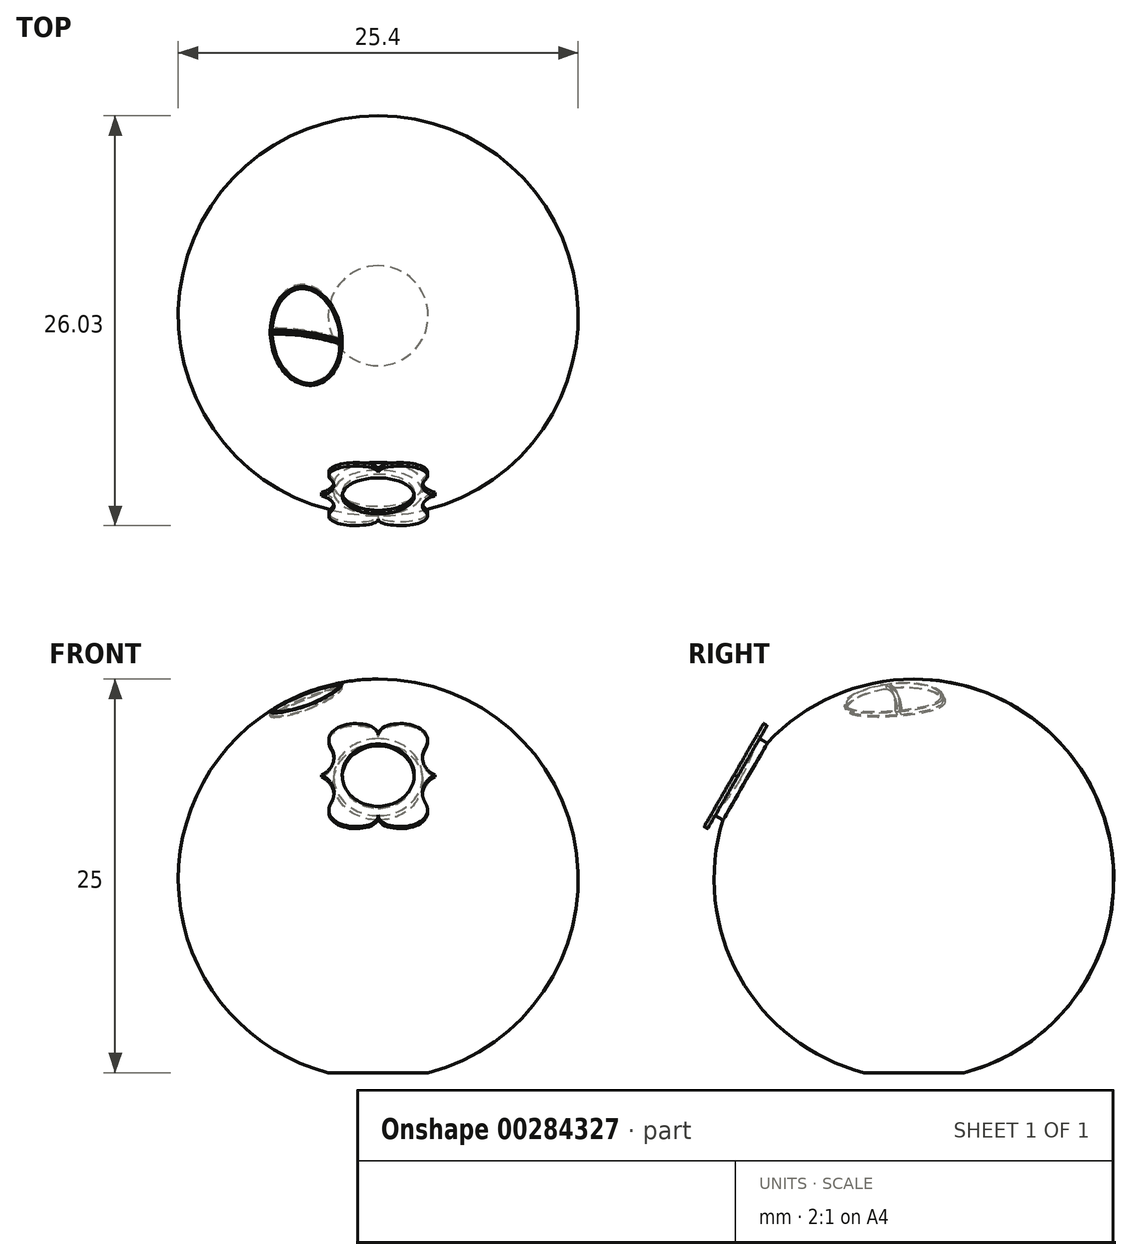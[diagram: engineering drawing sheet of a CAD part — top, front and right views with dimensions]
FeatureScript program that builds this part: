
annotation { "Feature Type Name" : "Feature", "Feature Type Description" : "" }
export const myFeature = defineFeature(function(context is Context, id is Id, definition is map)
    precondition{}
    {
        {
            var Q0;
            Q0=qCreatedBy(makeId("Right.planeOp"),FACE);
            var sketch = newSketch(context, id + "F0", { "sketchPlane" : qUnion([Q0])});
            skArc(sketch, "E0", {"start": v(3.18, 0) * mm, "mid": v(0, 25) * mm, "end": v(-3.18, 0) * mm});
            skLineSegment(sketch, "E1", {"start": v(3.18, 0) * mm, "end": v(-3.18, 0) * mm});
            skLineSegment(sketch, "E2", {"start": v(0, 25) * mm, "end": v(0, 0) * mm});
            skLineSegment(sketch, "E3", {"start": v(-11, 18.65) * mm, "end": v(-11.44, 18.9) * mm});
            skLineSegment(sketch, "E4", {"start": v(-11.44, 18.9) * mm, "end": v(-12.85, 16.46) * mm});
            skLineSegment(sketch, "E5", {"start": v(-12.85, 16.46) * mm, "end": v(-12.13, 16.04) * mm});
            skLineSegment(sketch, "E6", {"start": v(-12.58, 16.92) * mm, "end": v(-12.36, 16.8) * mm});
            skArc(sketch, "E7", {"start": v(-12.36, 16.8) * mm, "mid": v(-11.64, 17.7) * mm, "end": v(-11.02, 18.66) * mm});
            skLineSegment(sketch, "E8", {"start": v(-11.02, 18.66) * mm, "end": v(-12.43, 16.22) * mm, "construction": true});
            skLineSegment(sketch, "E9", {"start": v(-4.55, 24.15) * mm, "end": v(0, 12.3) * mm, "construction": true});
            skArc(sketch, "E10.0", {"start": v(3.11, 0.25) * mm, "mid": v(0, 24.74) * mm, "end": v(-3.11, 0.25) * mm});
            skLineSegment(sketch, "E11", {"start": v(-3.11, 0.25) * mm, "end": v(3.11, 0.25) * mm});
            skSolve(sketch);
        }
        {
            var Q0;
            {var subQ3=sQuery(id+"F0.wireOp",EDGE,"E2");Q0=makeQuery(id+"F0.imprint","IMPRINT",FACE,{"disambiguationData":[TD([[makeQuery(id+"F0.imprint","IMPRINT",EDGE,{"derivedFrom":subQ3}),-1.0]])]});}
            var Q1;
            {var subQ0=sQuery(id+"F0.wireOp",EDGE,"E10.0");var subQ1=sQuery(id+"F0.wireOp",EDGE,"E2");var subQ2=makeQuery(id+"F0.imprint","INTERSECT",VERTEX,{"derivedFrom":[subQ1,subQ0]});Q1=makeQuery(id+"F0.imprint","IMPRINT",FACE,{"disambiguationData":[TD([[makeQuery(id+"F0.imprint","IMPRINT",EDGE,{"disambiguationData":[TD([[subQ2,-1.0]])],"derivedFrom":subQ1}),-1.0]])]});}
            var Q2;
            Q2=sQuery(id+"F0.wireOp",EDGE,"E2");
            revolve(context, id + "F1", {"entities" : qUnion([Q0, Q1]), "axis" : qUnion([Q2]), "revolveType" : RevolveType.FULL});
        }
        {
            var Q0;
            {var subQ1=sQuery(id+"F0.wireOp",EDGE,"E5");Q0=makeQuery(id+"F0.imprint","IMPRINT",FACE,{"disambiguationData":[TD([[makeQuery(id+"F0.imprint","IMPRINT",EDGE,{"derivedFrom":subQ1}),1.0]])]});}
            var Q1;
            {var subQ4=sQuery(id+"F0.wireOp",EDGE,"E6");Q1=makeQuery(id+"F0.imprint","IMPRINT",FACE,{"disambiguationData":[TD([[makeQuery(id+"F0.imprint","IMPRINT",EDGE,{"derivedFrom":subQ4}),1.0]])]});}
            var Q2;
            Q2=sQuery(id+"F0.wireOp",EDGE,"E3");
            revolve(context, id + "F2", {"operationType" : NewBodyOperationType.ADD, "entities" : qUnion([Q0, Q1]), "axis" : qUnion([Q2]), "revolveType" : RevolveType.FULL});
        }
        {
            var Q0;
            Q0=makeQuery(id+"F2.opRevolve","SWEPT_FACE",FACE,{"disambiguationData":[OSD([sQuery(id+"F0.wireOp",EDGE,"E4")])]});
            var sketch = newSketch(context, id + "F3", { "sketchPlane" : qUnion([Q0])});
            skLineSegment(sketch, "E12", {"start": v(0, 10.65) * mm, "end": v(-3.6, 10.65) * mm});
            skLineSegment(sketch, "E13", {"start": v(0, 10.65) * mm, "end": v(0, 13.59) * mm});
            skArc(sketch, "E14", {"start": v(-3.6, 10.65) * mm, "mid": v(-2.88, 11.52) * mm, "end": v(-2.98, 12.65) * mm});
            skLineSegment(sketch, "E15", {"start": v(-3.6, 10.65) * mm, "end": v(0, 12.55) * mm});
            skLineSegment(sketch, "E16", {"start": v(-2.98, 12.65) * mm, "end": v(-2.29, 11.34) * mm, "construction": true});
            skFitSpline(sketch, "E17", {"points": [v(-2.98, 12.65) * mm, v(-2.15, 14.32) * mm, v(0, 13.59) * mm], "startDerivative": vector(-2.55, 4.82) * mm, "endDerivative": vector(0, -4.4) * mm});
            skSolve(sketch);
        }
        {
            var Q0;
            {var subQ1=sQuery(id+"F3.wireOp",EDGE,"E14");Q0=makeQuery(id+"F3.imprint","IMPRINT",FACE,{"disambiguationData":[TD([[makeQuery(id+"F3.imprint","IMPRINT",EDGE,{"derivedFrom":subQ1}),-1.0]])]});}
            var Q1;
            {var subQ0=sQuery(id+"F3.wireOp",EDGE,"E15");var subQ1=sQuery(id+"F3.wireOp",EDGE,"E12");var subQ2=makeQuery(id+"F3.imprint","INTERSECT",VERTEX,{"derivedFrom":[subQ1,sQuery(id+"F3.wireOp",EDGE,"E14"),subQ0]});Q1=makeQuery(id+"F3.imprint","IMPRINT",FACE,{"disambiguationData":[TD([[makeQuery(id+"F3.imprint","IMPRINT",EDGE,{"disambiguationData":[TD([[subQ2,1.0]])],"derivedFrom":subQ1}),-1.0]])]});}
            extrude(context, id + "F4", {"entities" : qUnion([Q0, Q1]), "oppositeDirection" : true, "depth" : 0.25 * mm});
        }
        {
            var Q0;
            Q0=makeQuery(id+"F4.opExtrude","SWEPT_BODY",BODY,{"disambiguationData":[OSD([sQuery(id+"F0.wireOp",EDGE,"E4"),sQuery(id+"F0.wireOp",EDGE,"E5"),sQuery(id+"F3.wireOp",EDGE,"E12"),sQuery(id+"F3.wireOp",EDGE,"E13"),sQuery(id+"F3.wireOp",EDGE,"E14"),sQuery(id+"F3.wireOp",EDGE,"E17")])]});
            var Q1;
            Q1=makeQuery(id+"Fticf5Y9S86viFH_1.opRevolve","SWEPT_BODY",BODY,{"disambiguationData":[OSD([sQuery(id+"F0.wireOp",EDGE,"E4"),sQuery(id+"F0.wireOp",EDGE,"E6"),sQuery(id+"F3.wireOp",EDGE,"E13"),sQuery(id+"F3.wireOp",EDGE,"E14"),sQuery(id+"F3.wireOp",EDGE,"E15"),sQuery(id+"F3.wireOp",EDGE,"E17")])]});
            var Q2;
            Q2=makeQuery(id+"F4.opExtrude","SWEPT_FACE",FACE,{"disambiguationData":[OSD([sQuery(id+"F3.wireOp",EDGE,"E12")])]});
            mirror(context, id + "F5", {"entities" : qUnion([Q0, Q1]), "mirrorPlane" : qUnion([Q2])});
        }
        {
            var Q0;
            Q0=makeQuery(id+"F4.opExtrude","SWEPT_BODY",BODY,{"disambiguationData":[OSD([sQuery(id+"F0.wireOp",EDGE,"E4"),sQuery(id+"F0.wireOp",EDGE,"E5"),sQuery(id+"F3.wireOp",EDGE,"E12"),sQuery(id+"F3.wireOp",EDGE,"E13"),sQuery(id+"F3.wireOp",EDGE,"E14"),sQuery(id+"F3.wireOp",EDGE,"E17")])]});
            var Q1;
            Q1=makeQuery(id+"F5.opPattern","COPY",BODY,{"derivedFrom":makeQuery(id+"F4.opExtrude","SWEPT_BODY",BODY,{"disambiguationData":[OSD([sQuery(id+"F0.wireOp",EDGE,"E4"),sQuery(id+"F0.wireOp",EDGE,"E5"),sQuery(id+"F3.wireOp",EDGE,"E12"),sQuery(id+"F3.wireOp",EDGE,"E13"),sQuery(id+"F3.wireOp",EDGE,"E14"),sQuery(id+"F3.wireOp",EDGE,"E17")])]}),"instanceName":"1"});
            var Q2;
            Q2=makeQuery(id+"F5.opPattern","COPY",BODY,{"derivedFrom":makeQuery(id+"Fticf5Y9S86viFH_1.opRevolve","SWEPT_BODY",BODY,{"disambiguationData":[OSD([sQuery(id+"F0.wireOp",EDGE,"E4"),sQuery(id+"F0.wireOp",EDGE,"E5"),sQuery(id+"F3.wireOp",EDGE,"E13"),sQuery(id+"F3.wireOp",EDGE,"E14"),sQuery(id+"F3.wireOp",EDGE,"E15"),sQuery(id+"F3.wireOp",EDGE,"E17")])]}),"instanceName":"1"});
            var Q3;
            Q3=makeQuery(id+"Fticf5Y9S86viFH_1.opRevolve","SWEPT_BODY",BODY,{"disambiguationData":[OSD([sQuery(id+"F0.wireOp",EDGE,"E4"),sQuery(id+"F0.wireOp",EDGE,"E5"),sQuery(id+"F3.wireOp",EDGE,"E13"),sQuery(id+"F3.wireOp",EDGE,"E14"),sQuery(id+"F3.wireOp",EDGE,"E15"),sQuery(id+"F3.wireOp",EDGE,"E17")])]});
            var Q4;
            Q4=qCreatedBy(makeId("Right.planeOp"),FACE);
            mirror(context, id + "F6", {"operationType" : NewBodyOperationType.ADD, "entities" : qUnion([Q0, Q1, Q2, Q3]), "mirrorPlane" : qUnion([Q4])});
        }
        {
            var Q0;
            {var subQ4=sQuery(id+"F0.wireOp",EDGE,"E6");Q0=makeQuery(id+"F0.imprint","IMPRINT",FACE,{"disambiguationData":[TD([[makeQuery(id+"F0.imprint","IMPRINT",EDGE,{"derivedFrom":subQ4}),1.0]])]});}
            var Q1;
            Q1=sQuery(id+"F0.wireOp",EDGE,"E3");
            revolve(context, id + "F7", {"operationType" : NewBodyOperationType.REMOVE, "entities" : qUnion([Q0]), "axis" : qUnion([Q1]), "revolveType" : RevolveType.FULL, "oppositeDirection" : true});
        }
        {
            var Q0;
            Q0=sQuery(id+"F0.wireOp",EDGE,"E9");
            var Q1;
            Q1=sQuery(id+"F0.wireOp",VERTEX,"E9.start");
            cPlane(context, id + "F8", {"entities" : qUnion([Q0, Q1]), "cplaneType" : CPlaneType.LINE_POINT, "offset" : 25.4 * mm, "width" : 152.4 * mm, "height" : 152.4 * mm});
        }
        {
            var Q0;
            Q0=qCreatedBy(id+"F8.planeOp",FACE);
            var sketch = newSketch(context, id + "F9", { "sketchPlane" : qUnion([Q0])});
            skCircle(sketch, "E18", {"center": v(-4.57, -7.28) * mm, "radius": 3.05 * mm, "construction": true});
            skArc(sketch, "E19", {"start": v(-1.65, -7.15) * mm, "mid": v(-4.57, -4.36) * mm, "end": v(-7.5, -7.15) * mm, "construction": true});
            skLineSegment(sketch, "E20", {"start": v(-7.5, -7.4) * mm, "end": v(-1.65, -7.4) * mm, "construction": true});
            skLineSegment(sketch, "E21", {"start": v(-1.65, -7.15) * mm, "end": v(-7.5, -7.15) * mm, "construction": true});
            skLineSegment(sketch, "E22", {"start": v(-4.57, -7.4) * mm, "end": v(-4.57, -7.15) * mm, "construction": true});
            skArc(sketch, "E23.trimOffspring", {"start": v(-7.5, -7.4) * mm, "mid": v(-4.57, -10.2) * mm, "end": v(-1.65, -7.4) * mm, "construction": true});
            skCircle(sketch, "E24", {"center": v(-4.16, -9.44) * mm, "radius": 0.38 * mm});
            skLineSegment(sketch, "E25", {"start": v(0, -0.57) * mm, "end": v(0, -11.54) * mm, "construction": true});
            skCircle(sketch, "E26", {"center": v(4.57, -7.28) * mm, "radius": 3.05 * mm});
            skLineSegment(sketch, "E27", {"start": v(-4.57, -7.28) * mm, "end": v(4.57, -7.28) * mm, "construction": true});
            skPoint(sketch, "E28", {"position": v(0, -7.28) * mm});
            skCircle(sketch, "E29", {"center": v(4.99, -9.44) * mm, "radius": 0.38 * mm});
            skLineSegment(sketch, "E30", {"start": v(-4.16, -9.44) * mm, "end": v(4.99, -9.44) * mm, "construction": true});
            skArc(sketch, "E31", {"start": v(-1.65, -7.4) * mm, "mid": v(-4.57, -7.15) * mm, "end": v(-7.5, -7.4) * mm, "construction": true});
            skArc(sketch, "E32", {"start": v(-1.65, -7.15) * mm, "mid": v(-4.57, -6.9) * mm, "end": v(-7.5, -7.15) * mm, "construction": true});
            skEllipse(sketch, "E33", {"center": v(-4.57, -7.28) * mm, "majorRadius": 3.05 * mm, "minorRadius": 2.29 * mm, "majorAxis": v(0, 1)});
            skEllipticalArc(sketch, "E34", {});
            skArc(sketch, "E35", {"start": v(-6.73, -7.4) * mm, "mid": v(-4.57, -7.66) * mm, "end": v(-2.42, -7.4) * mm});
            skArc(sketch, "E36", {"start": v(-6.73, -7.15) * mm, "mid": v(-4.57, -7.4) * mm, "end": v(-2.42, -7.15) * mm});
            skEllipticalArc(sketch, "E37.trimOffspring", {});
            skEllipticalArc(sketch, "E38.trimOffspring", {});
            const initialGuessF9  = {"E34": [-0.004572, -0.007277323653828481, 0, -1, 0.002921, 0.002159, 4.755880951174804, 1.5273043560047805], "E37.trimOffspring": [-0.004572, -0.007277323653828481, 0, -1, 0.002921, 0.002159, 1.6142882975850121, 4.668897009594579], "E38.trimOffspring": [-0.004572, -0.007277323653828481, 0, -1, 0.002921, 0.002159, 1.5668431296332357, 1.5707963267948966]};
            skSetInitialGuess(sketch, initialGuessF9);
            skSolve(sketch);
        }
        {
            var Q0;
            Q0=makeQuery(id+"F9.imprint","IMPRINT",FACE,{"disambiguationData":[TD([[makeQuery(id+"F9.imprint","IMPRINT",EDGE,{"derivedFrom":sQuery(id+"F9.wireOp",EDGE,"E33")}),1.0]])]});
            extrude(context, id + "F10", {"entities" : qUnion([Q0]), "operationType" : NewBodyOperationType.REMOVE, "depth" : 5.08 * mm});
        }
        {
            var Q0;
            {var subQ0=sQuery(id+"F0.wireOp",EDGE,"E10.0");var subQ1=sQuery(id+"F0.wireOp",EDGE,"E2");var subQ2=makeQuery(id+"F0.imprint","INTERSECT",VERTEX,{"derivedFrom":[subQ1,subQ0]});Q0=makeQuery(id+"F0.imprint","IMPRINT",FACE,{"disambiguationData":[TD([[makeQuery(id+"F0.imprint","IMPRINT",EDGE,{"disambiguationData":[TD([[subQ2,-1.0]])],"derivedFrom":subQ1}),-1.0]])]});}
            var Q1;
            Q1=sQuery(id+"F0.wireOp",EDGE,"E2");
            revolve(context, id + "F11", {"operationType" : NewBodyOperationType.ADD, "entities" : qUnion([Q0]), "axis" : qUnion([Q1]), "revolveType" : RevolveType.FULL});
        }
    });
